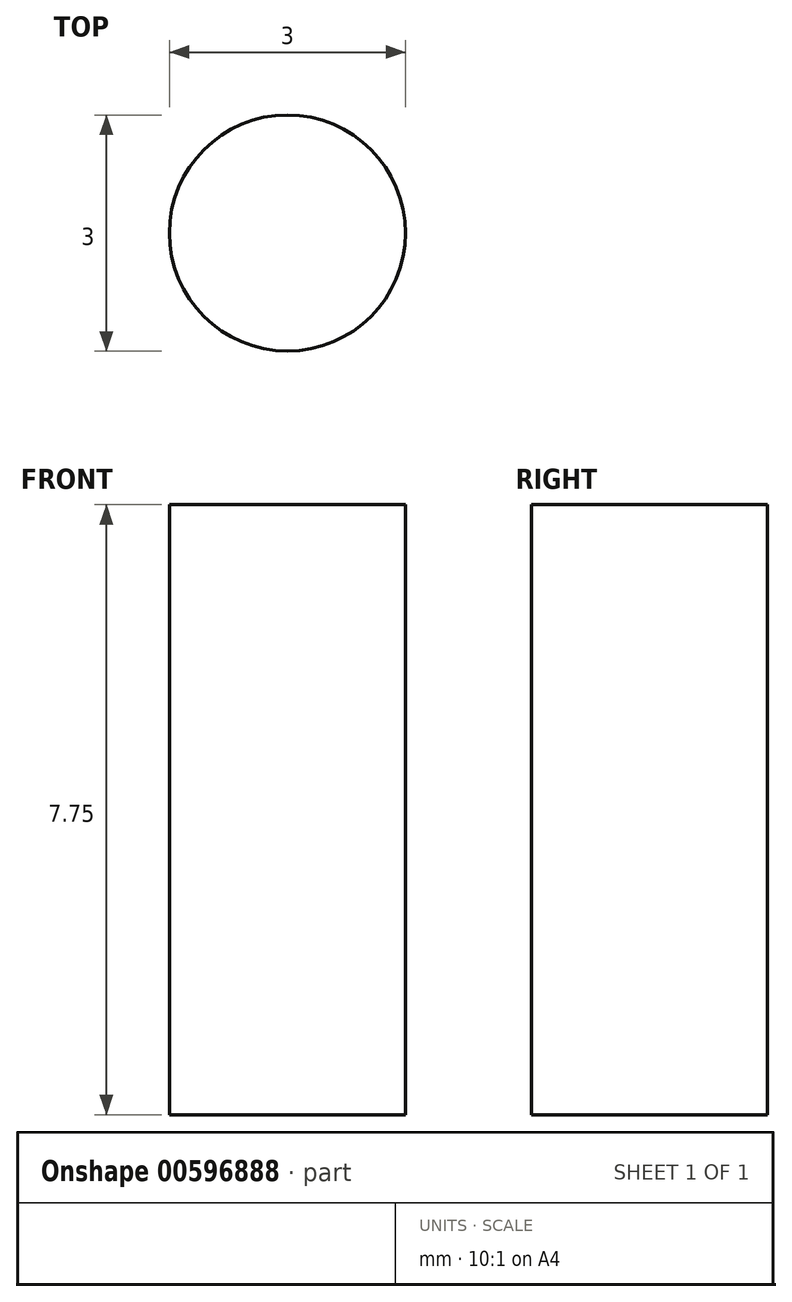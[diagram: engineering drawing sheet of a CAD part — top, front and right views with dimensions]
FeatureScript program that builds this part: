
annotation { "Feature Type Name" : "Feature", "Feature Type Description" : "" }
export const myFeature = defineFeature(function(context is Context, id is Id, definition is map)
    precondition{}
    {
        {
            var Q0;
            Q0=qCreatedBy(makeId("Top.planeOp"),FACE);
            var sketch = newSketch(context, id + "F0", { "sketchPlane" : qUnion([Q0])});
            skCircle(sketch, "E0", {"center": v(0, 0) * mm, "radius": 9 * mm, "construction": true});
            skCircle(sketch, "E1", {"center": v(0, 0) * mm, "radius": 1.5 * mm});
            skSolve(sketch);
        }
        {
            var Q0;
            Q0=sQuery(id+"F0.wireOp",EDGE,"E1");
            extrude(context, id + "F1", {"bodyType" : ToolBodyType.SURFACE, "surfaceEntities" : qUnion([Q0]), "depth" : 7.75 * mm, "offsetDistance" : 25.4 * mm});
        }
    });
